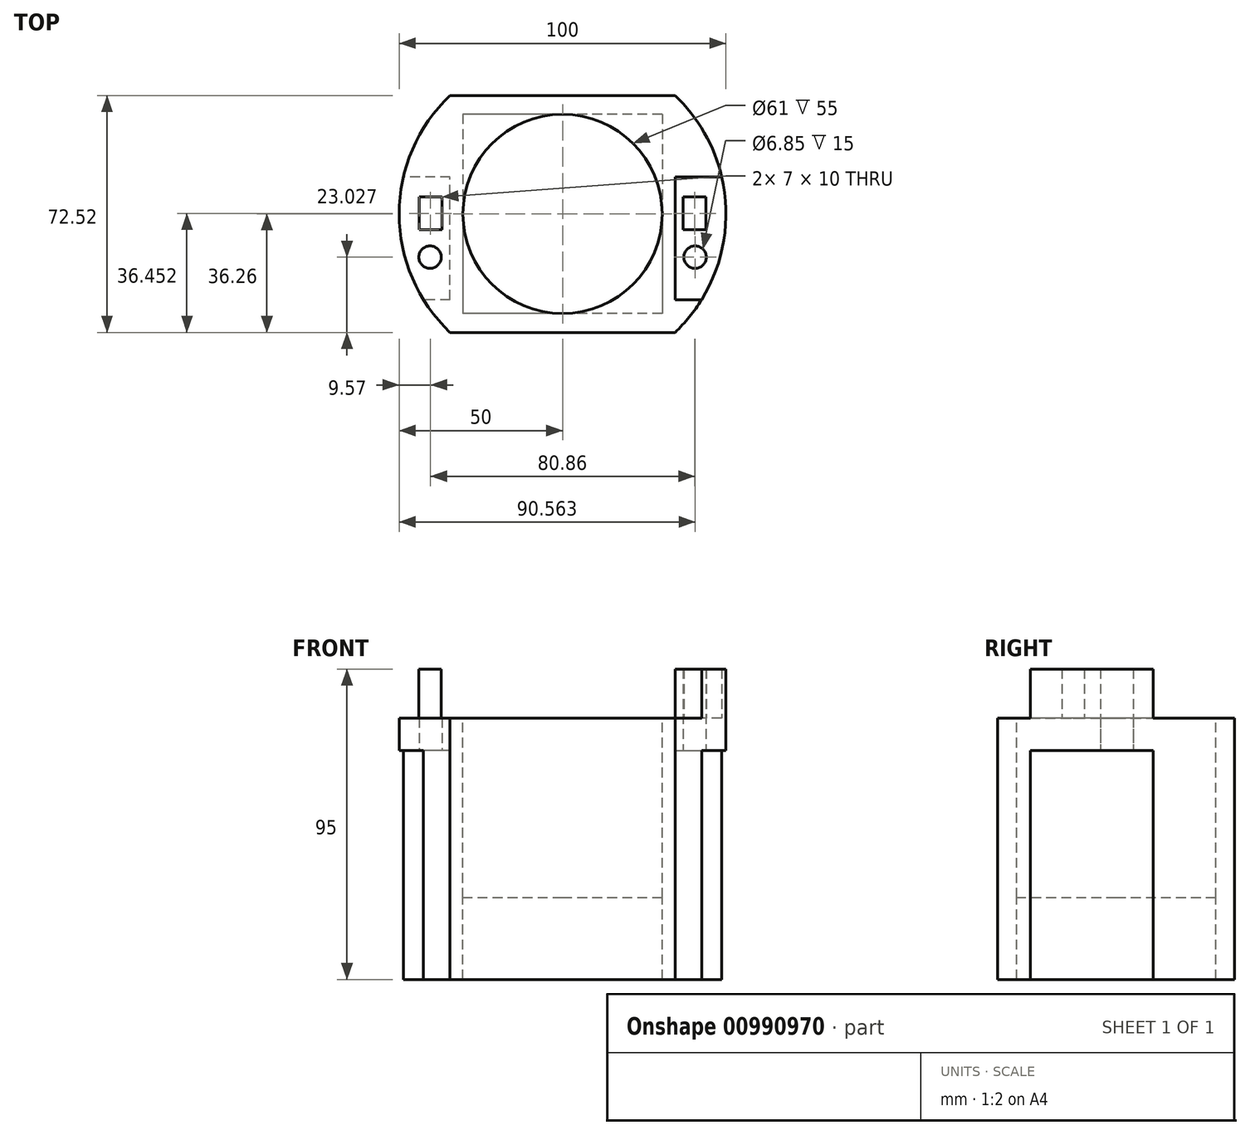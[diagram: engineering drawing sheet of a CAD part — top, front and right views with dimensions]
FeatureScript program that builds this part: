
annotation { "Feature Type Name" : "Feature", "Feature Type Description" : "" }
export const myFeature = defineFeature(function(context is Context, id is Id, definition is map)
    precondition{}
    {
        {
            var Q0;
            Q0=qCreatedBy(makeId("Top.planeOp"),FACE);
            var sketch = newSketch(context, id + "F0", { "sketchPlane" : qUnion([Q0])});
            skCircle(sketch, "E0", {"center": v(-40.56, -13.23) * mm, "radius": 3.43 * mm});
            skLineSegment(sketch, "E1", {"start": v(0, 50.2) * mm, "end": v(0, -49.8) * mm, "construction": true});
            skCircle(sketch, "E2.MirrorC", {"center": v(40.56, -13.23) * mm, "radius": 3.43 * mm});
            skLineSegment(sketch, "E3.bottom", {"start": v(-36.93, -4.8) * mm, "end": v(-43.93, -4.8) * mm});
            skLineSegment(sketch, "E3.top", {"start": v(-36.93, 5.2) * mm, "end": v(-43.93, 5.2) * mm});
            skLineSegment(sketch, "E3.left", {"start": v(-36.93, -4.8) * mm, "end": v(-36.93, 5.2) * mm});
            skLineSegment(sketch, "E3.right", {"start": v(-43.93, -4.8) * mm, "end": v(-43.93, 5.2) * mm});
            skLineSegment(sketch, "E4.MirrorCS", {"start": v(36.93, 5.2) * mm, "end": v(43.93, 5.2) * mm});
            skLineSegment(sketch, "E5.MirrorCS", {"start": v(36.93, -4.8) * mm, "end": v(36.93, 5.2) * mm});
            skLineSegment(sketch, "E6.MirrorCS", {"start": v(36.93, -4.8) * mm, "end": v(43.93, -4.8) * mm});
            skLineSegment(sketch, "E7.MirrorCS", {"start": v(43.93, -4.8) * mm, "end": v(43.93, 5.2) * mm});
            skCircle(sketch, "E8", {"center": v(0, 0) * mm, "radius": 30.5 * mm});
            skCircle(sketch, "E9", {"center": v(0, 0) * mm, "radius": 50 * mm});
            skLineSegment(sketch, "E10.bottom", {"start": v(34.43, -36.26) * mm, "end": v(-34.43, -36.26) * mm});
            skLineSegment(sketch, "E10.top", {"start": v(34.43, 36.26) * mm, "end": v(-34.43, 36.26) * mm});
            skLineSegment(sketch, "E10.left", {"start": v(34.43, -36.26) * mm, "end": v(34.43, 36.26) * mm});
            skLineSegment(sketch, "E10.right", {"start": v(-34.43, -36.26) * mm, "end": v(-34.43, 36.26) * mm});
            skLineSegment(sketch, "E11", {"start": v(-34.43, 11.26) * mm, "end": v(-48.72, 11.26) * mm});
            skLineSegment(sketch, "E12", {"start": v(-34.43, -26.26) * mm, "end": v(-42.55, -26.26) * mm});
            skLineSegment(sketch, "E13.MirrorCS", {"start": v(34.43, 11.26) * mm, "end": v(48.72, 11.26) * mm});
            skLineSegment(sketch, "E14.MirrorCS", {"start": v(34.43, -26.26) * mm, "end": v(42.55, -26.26) * mm});
            skSolve(sketch);
        }
        {
            var Q0;
            Q0=makeQuery(id+"F0.imprint","IMPRINT",FACE,{"disambiguationData":[TD([[makeQuery(id+"F0.imprint","IMPRINT",EDGE,{"derivedFrom":sQuery(id+"F0.wireOp",EDGE,"E8")}),-1.0]])]});
            var Q1;
            {var subQ3=sQuery(id+"F0.wireOp",EDGE,"E11");Q1=makeQuery(id+"F0.imprint","IMPRINT",FACE,{"disambiguationData":[TD([[makeQuery(id+"F0.imprint","IMPRINT",EDGE,{"derivedFrom":subQ3}),-1.0]])]});}
            var Q2;
            {var subQ3=sQuery(id+"F0.wireOp",EDGE,"E13.MirrorCS");Q2=makeQuery(id+"F0.imprint","IMPRINT",FACE,{"disambiguationData":[TD([[makeQuery(id+"F0.imprint","IMPRINT",EDGE,{"derivedFrom":subQ3}),1.0]])]});}
            var Q3;
            {var subQ3=sQuery(id+"F0.wireOp",EDGE,"E14.MirrorCS");Q3=makeQuery(id+"F0.imprint","IMPRINT",FACE,{"disambiguationData":[TD([[makeQuery(id+"F0.imprint","IMPRINT",EDGE,{"derivedFrom":subQ3}),-1.0]])]});}
            var Q4;
            {var subQ3=sQuery(id+"F0.wireOp",EDGE,"E12");Q4=makeQuery(id+"F0.imprint","IMPRINT",FACE,{"disambiguationData":[TD([[makeQuery(id+"F0.imprint","IMPRINT",EDGE,{"derivedFrom":subQ3}),1.0]])]});}
            extrude(context, id + "F1", {"entities" : qUnion([Q0, Q1, Q2, Q3, Q4]), "oppositeDirection" : true, "depth" : 45 * mm, "offsetDistance" : 25 * mm});
        }
        {
            var Q0;
            Q0=makeQuery(id+"F0.imprint","IMPRINT",FACE,{"disambiguationData":[TD([[makeQuery(id+"F0.imprint","IMPRINT",EDGE,{"derivedFrom":sQuery(id+"F0.wireOp",EDGE,"e0b62fb5-1751-473e-acd3-66306070ded0.bottom")}),1.0]])]});
            var Q1;
            Q1=makeQuery(id+"F0.imprint","IMPRINT",FACE,{"disambiguationData":[TD([[makeQuery(id+"F0.imprint","IMPRINT",EDGE,{"derivedFrom":sQuery(id+"F0.wireOp",EDGE,"E0")}),1.0]])]});
            var Q2;
            Q2=makeQuery(id+"F0.imprint","IMPRINT",FACE,{"disambiguationData":[TD([[makeQuery(id+"F0.imprint","IMPRINT",EDGE,{"derivedFrom":sQuery(id+"F0.wireOp",EDGE,"E2.MirrorC")}),-1.0]])]});
            var Q3;
            Q3=makeQuery(id+"F0.imprint","IMPRINT",FACE,{"disambiguationData":[TD([[makeQuery(id+"F0.imprint","IMPRINT",EDGE,{"derivedFrom":sQuery(id+"F0.wireOp",EDGE,"E8")}),-1.0]])]});
            var Q4;
            Q4=makeQuery(id+"F0.imprint","IMPRINT",FACE,{"disambiguationData":[TD([[makeQuery(id+"F0.imprint","IMPRINT",EDGE,{"derivedFrom":sQuery(id+"F0.wireOp",EDGE,"E0")}),-1.0]])]});
            var Q5;
            Q5=makeQuery(id+"F0.imprint","IMPRINT",FACE,{"disambiguationData":[TD([[makeQuery(id+"F0.imprint","IMPRINT",EDGE,{"derivedFrom":sQuery(id+"F0.wireOp",EDGE,"E2.MirrorC")}),1.0]])]});
            var Q6;
            {var subQ3=sQuery(id+"F0.wireOp",EDGE,"E13.MirrorCS");Q6=makeQuery(id+"F0.imprint","IMPRINT",FACE,{"disambiguationData":[TD([[makeQuery(id+"F0.imprint","IMPRINT",EDGE,{"derivedFrom":subQ3}),1.0]])]});}
            var Q7;
            {var subQ3=sQuery(id+"F0.wireOp",EDGE,"E14.MirrorCS");Q7=makeQuery(id+"F0.imprint","IMPRINT",FACE,{"disambiguationData":[TD([[makeQuery(id+"F0.imprint","IMPRINT",EDGE,{"derivedFrom":subQ3}),-1.0]])]});}
            var Q8;
            {var subQ3=sQuery(id+"F0.wireOp",EDGE,"E12");Q8=makeQuery(id+"F0.imprint","IMPRINT",FACE,{"disambiguationData":[TD([[makeQuery(id+"F0.imprint","IMPRINT",EDGE,{"derivedFrom":subQ3}),1.0]])]});}
            var Q9;
            {var subQ3=sQuery(id+"F0.wireOp",EDGE,"E11");Q9=makeQuery(id+"F0.imprint","IMPRINT",FACE,{"disambiguationData":[TD([[makeQuery(id+"F0.imprint","IMPRINT",EDGE,{"derivedFrom":subQ3}),-1.0]])]});}
            extrude(context, id + "F2", {"entities" : qUnion([Q0, Q1, Q2, Q3, Q4, Q5, Q6, Q7, Q8, Q9]), "operationType" : NewBodyOperationType.ADD, "depth" : 10 * mm, "offsetDistance" : 25 * mm});
        }
        {
            var Q0;
            Q0=makeQuery(id+"F0.imprint","IMPRINT",FACE,{"disambiguationData":[TD([[makeQuery(id+"F0.imprint","IMPRINT",EDGE,{"derivedFrom":sQuery(id+"F0.wireOp",EDGE,"E0")}),1.0]])]});
            var Q1;
            Q1=makeQuery(id+"F0.imprint","IMPRINT",FACE,{"disambiguationData":[TD([[makeQuery(id+"F0.imprint","IMPRINT",EDGE,{"derivedFrom":sQuery(id+"F0.wireOp",EDGE,"E2.MirrorC")}),-1.0]])]});
            extrude(context, id + "F3", {"entities" : qUnion([Q0, Q1]), "operationType" : NewBodyOperationType.ADD, "depth" : 25 * mm, "offsetDistance" : 25 * mm});
        }
        {
            var Q0;
            Q0=makeQuery(id+"F1.opExtrude","CAP_FACE",FACE,{"disambiguationData":[OSD([sQuery(id+"F0.wireOp",EDGE,"E8"),sQuery(id+"F0.wireOp",EDGE,"E9"),sQuery(id+"F0.wireOp",EDGE,"E10.bottom"),sQuery(id+"F0.wireOp",EDGE,"E10.top"),sQuery(id+"F0.wireOp",EDGE,"E10.left"),sQuery(id+"F0.wireOp",EDGE,"E10.right"),sQuery(id+"F0.wireOp",EDGE,"E11"),sQuery(id+"F0.wireOp",EDGE,"E12"),sQuery(id+"F0.wireOp",EDGE,"E13.MirrorCS"),sQuery(id+"F0.wireOp",EDGE,"E14.MirrorCS")])],"isStart":false});
            var sketch = newSketch(context, id + "F4", { "sketchPlane" : qUnion([Q0])});
            skLineSegment(sketch, "E15.bottom", {"start": v(34.43, -36.26) * mm, "end": v(-34.43, -36.26) * mm});
            skLineSegment(sketch, "E15.top", {"start": v(34.43, 36.26) * mm, "end": v(-34.43, 36.26) * mm});
            skLineSegment(sketch, "E15.left", {"start": v(34.43, -36.26) * mm, "end": v(34.43, 36.26) * mm});
            skLineSegment(sketch, "E15.right", {"start": v(-34.43, -36.26) * mm, "end": v(-34.43, 36.26) * mm});
            skPoint(sketch, "E15.middle", {"position": v(0, 0) * mm});
            skLineSegment(sketch, "E16.bottom", {"start": v(50, -50) * mm, "end": v(-50, -50) * mm});
            skLineSegment(sketch, "E16.top", {"start": v(50, 50) * mm, "end": v(-50, 50) * mm});
            skLineSegment(sketch, "E16.left", {"start": v(50, -50) * mm, "end": v(50, 50) * mm});
            skLineSegment(sketch, "E16.right", {"start": v(-50, -50) * mm, "end": v(-50, 50) * mm});
            skLineSegment(sketch, "E17.bottom", {"start": v(30.5, 30.5) * mm, "end": v(-30.5, 30.5) * mm});
            skLineSegment(sketch, "E17.top", {"start": v(30.5, -30.5) * mm, "end": v(-30.5, -30.5) * mm});
            skLineSegment(sketch, "E17.left", {"start": v(-30.5, -30.5) * mm, "end": v(-30.5, 30.5) * mm});
            skLineSegment(sketch, "E17.right", {"start": v(30.5, -30.5) * mm, "end": v(30.5, 30.5) * mm});
            skSolve(sketch);
        }
        {
            var Q0;
            {var subQ16=sQuery(id+"F4.wireOp",EDGE,"E15.bottom");Q0=makeQuery(id+"F4.imprint","IMPRINT",FACE,{"disambiguationData":[TD([[makeQuery(id+"F4.imprint","IMPRINT",EDGE,{"derivedFrom":subQ16}),-1.0]])]});}
            var Q1;
            {var subQ0=sQuery(id+"F4.wireOp",EDGE,"E15.left");var subQ2=sQuery(id+"F0.wireOp",EDGE,"E13.MirrorCS");var subQ5=makeQuery(id+"F1.opExtrude","CAP_EDGE",EDGE,{"disambiguationData":[OSD([subQ2])],"isStart":false});var subQ6=makeQuery(id+"F4.imprint","INTERSECT",VERTEX,{"derivedFrom":[subQ5,subQ0]});Q1=makeQuery(id+"F4.imprint","IMPRINT",FACE,{"disambiguationData":[TD([[makeQuery(id+"F4.imprint","IMPRINT",EDGE,{"disambiguationData":[TD([[subQ6,-1.0]])],"derivedFrom":subQ5}),-1.0]])]});}
            var Q2;
            {var subQ0=sQuery(id+"F4.wireOp",EDGE,"E15.right");var subQ2=sQuery(id+"F0.wireOp",EDGE,"E11");var subQ5=makeQuery(id+"F1.opExtrude","CAP_EDGE",EDGE,{"disambiguationData":[OSD([subQ2])],"isStart":false});var subQ6=makeQuery(id+"F4.imprint","INTERSECT",VERTEX,{"derivedFrom":[subQ5,subQ0]});Q2=makeQuery(id+"F4.imprint","IMPRINT",FACE,{"disambiguationData":[TD([[makeQuery(id+"F4.imprint","IMPRINT",EDGE,{"disambiguationData":[TD([[subQ6,-1.0]])],"derivedFrom":subQ5}),1.0]])]});}
            var Q3;
            {var subQ2=sQuery(id+"F0.wireOp",EDGE,"E12");var subQ4=makeQuery(id+"F1.opExtrude","CAP_EDGE",EDGE,{"disambiguationData":[OSD([subQ2])],"isStart":false});Q3=makeQuery(id+"F4.imprint","IMPRINT",FACE,{"disambiguationData":[TD([[makeQuery(id+"F4.imprint","IMPRINT",EDGE,{"derivedFrom":subQ4}),-1.0]])]});}
            var Q4;
            {var subQ2=sQuery(id+"F0.wireOp",EDGE,"E14.MirrorCS");var subQ4=makeQuery(id+"F1.opExtrude","CAP_EDGE",EDGE,{"disambiguationData":[OSD([subQ2])],"isStart":false});Q4=makeQuery(id+"F4.imprint","IMPRINT",FACE,{"disambiguationData":[TD([[makeQuery(id+"F4.imprint","IMPRINT",EDGE,{"derivedFrom":subQ4}),1.0]])]});}
            extrude(context, id + "F5", {"entities" : qUnion([Q0, Q1, Q2, Q3, Q4]), "operationType" : NewBodyOperationType.ADD, "depth" : 25 * mm, "offsetDistance" : 25 * mm});
        }
    });
